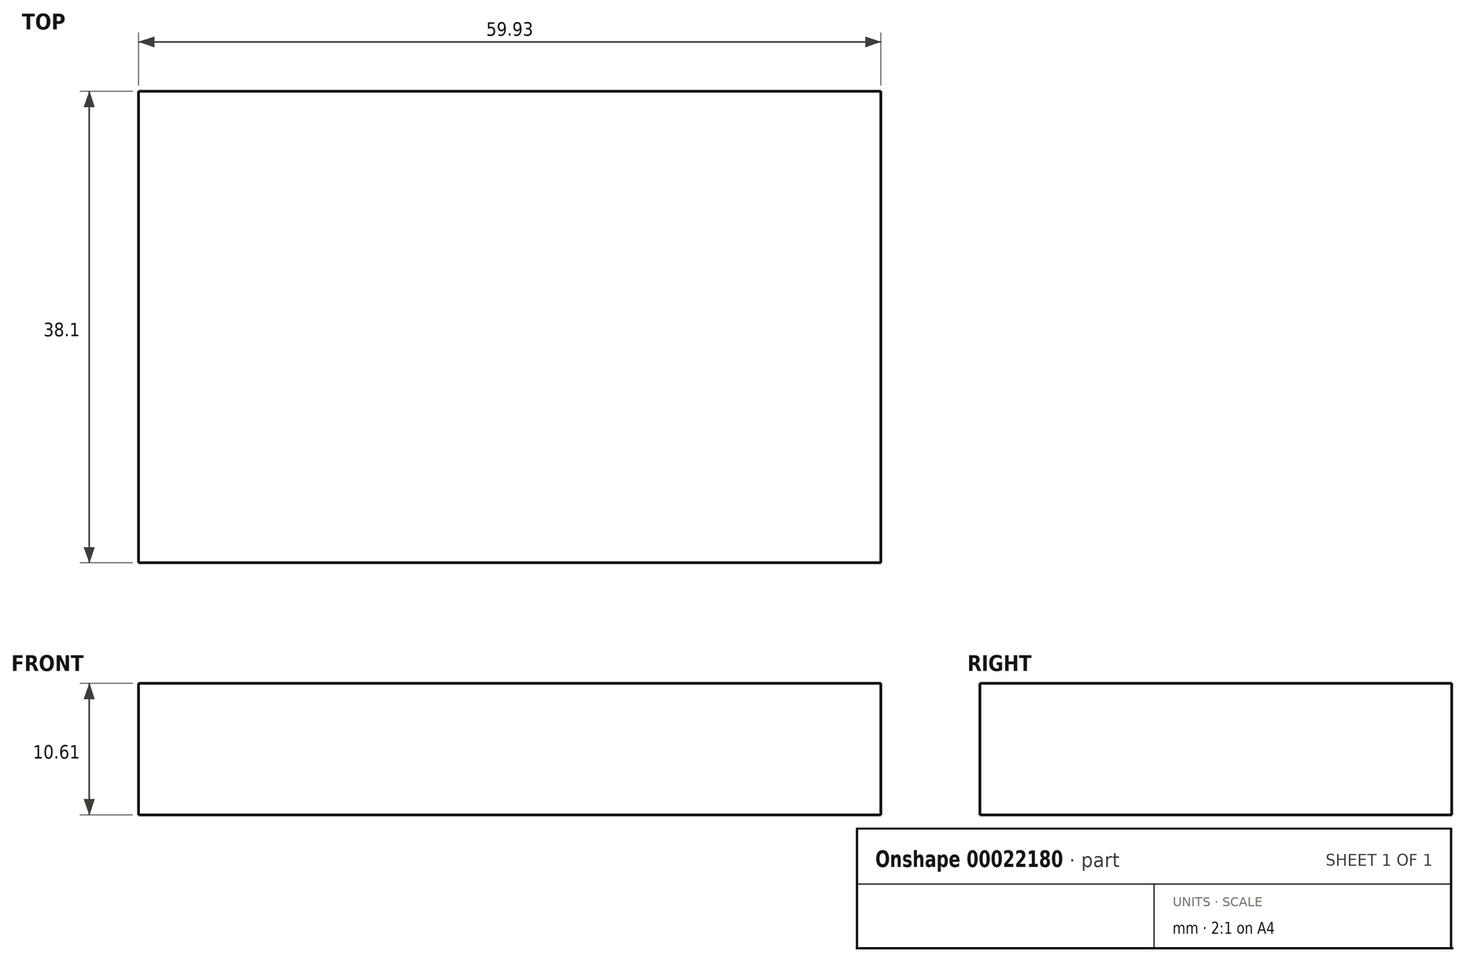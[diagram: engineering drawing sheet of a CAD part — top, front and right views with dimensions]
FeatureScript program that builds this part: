
annotation { "Feature Type Name" : "Feature", "Feature Type Description" : "" }
export const myFeature = defineFeature(function(context is Context, id is Id, definition is map)
    precondition{}
    {
        {
            var Q0;
            Q0=qCreatedBy(makeId("Front.planeOp"),FACE);
            var sketch = newSketch(context, id + "F0", { "sketchPlane" : qUnion([Q0])});
            skLineSegment(sketch, "E0", {"start": v(-27.24, -10.61) * mm, "end": v(32.7, -10.61) * mm});
            skLineSegment(sketch, "E1", {"start": v(-27.24, -10.61) * mm, "end": v(-27.24, 0) * mm});
            skLineSegment(sketch, "E2", {"start": v(-27.24, 0) * mm, "end": v(32.7, 0) * mm});
            skLineSegment(sketch, "E3", {"start": v(32.7, 0) * mm, "end": v(32.7, -10.61) * mm});
            skSolve(sketch);
        }
        {
            var Q0;
            Q0=makeQuery(id+"F0.imprint","IMPRINT",FACE,{"disambiguationData":[TD([[makeQuery(id+"F0.imprint","IMPRINT",EDGE,{"derivedFrom":sQuery(id+"F0.wireOp",EDGE,"E0")}),1.0]])]});
            extrude(context, id + "F1", {"entities" : qUnion([Q0]), "depth" : 38.1 * mm});
        }
    });
